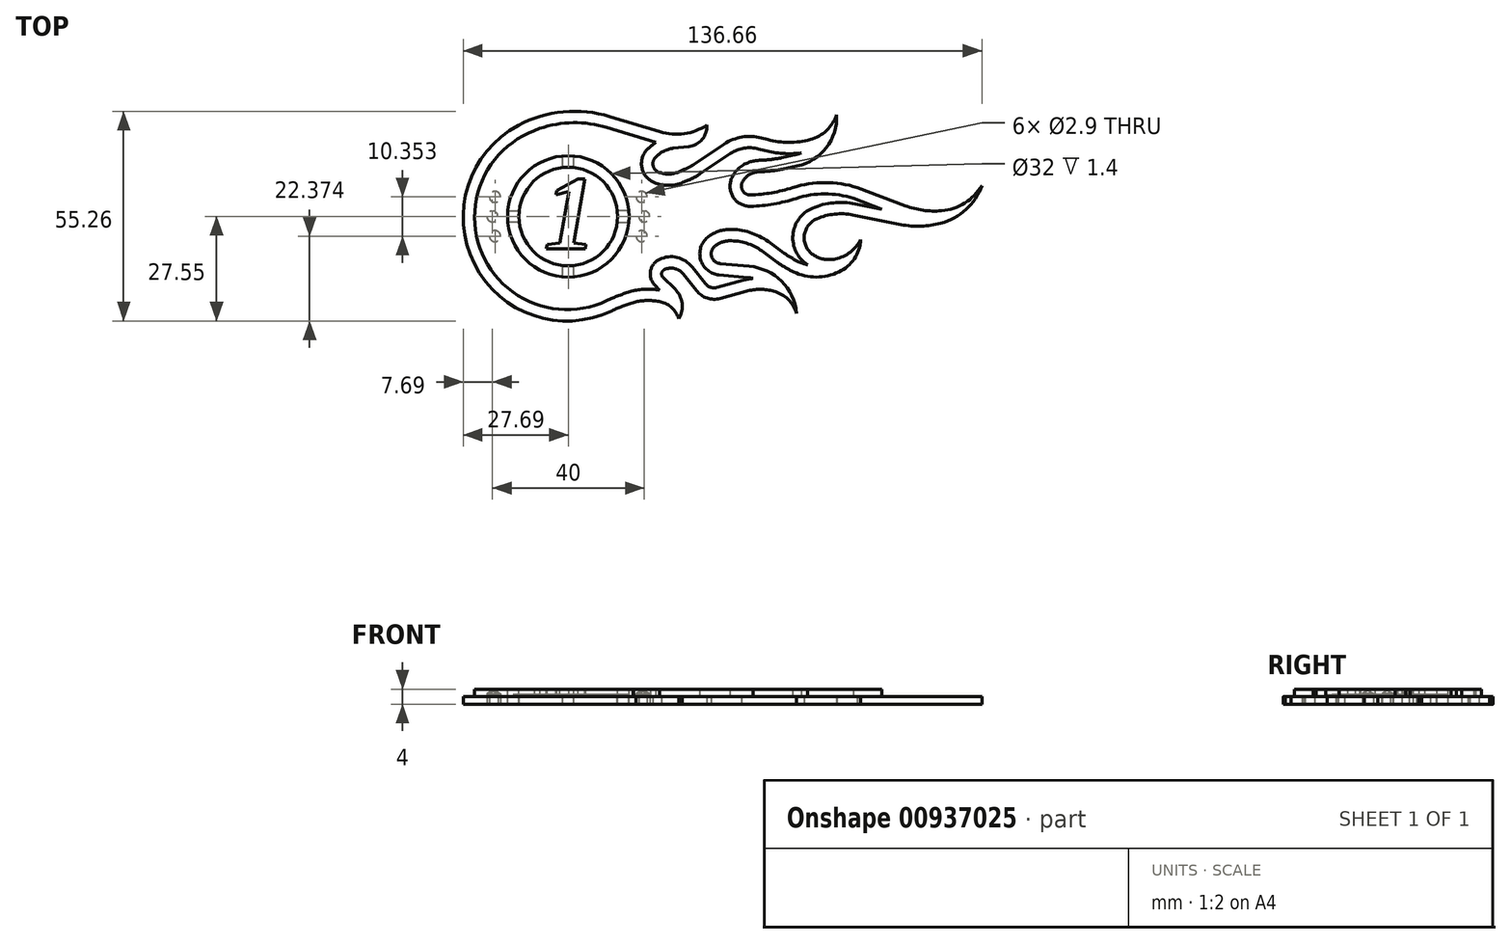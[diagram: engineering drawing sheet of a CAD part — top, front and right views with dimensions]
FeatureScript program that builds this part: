
annotation { "Feature Type Name" : "Feature", "Feature Type Description" : "" }
export const myFeature = defineFeature(function(context is Context, id is Id, definition is map)
    precondition{}
    {
        {
            var Q0;
            Q0=qCreatedBy(makeId("Top.planeOp"),FACE);
            var sketch = newSketch(context, id + "F0", { "sketchPlane" : qUnion([Q0])});
            skArc(sketch, "E0", {"start": v(-15.8, 20.8) * mm, "mid": v(-9.44, 20.3) * mm, "end": v(-3.49, 22.58) * mm});
            skLineSegment(sketch, "E1", {"start": v(-29, 24.82) * mm, "end": v(-15.8, 20.8) * mm});
            skArc(sketch, "E2", {"start": v(-53.14, 22.5) * mm, "mid": v(-64.76, -14.01) * mm, "end": v(-28.48, -26.36) * mm});
            skArc(sketch, "E3", {"start": v(-29, 24.82) * mm, "mid": v(-41.3, 26.06) * mm, "end": v(-53.14, 22.5) * mm});
            skArc(sketch, "E4", {"start": v(-8.25, 16.94) * mm, "mid": v(-4.75, 18.81) * mm, "end": v(-3.49, 22.58) * mm});
            skArc(sketch, "E5", {"start": v(-10.87, -28.44) * mm, "mid": v(-12.7, -25.58) * mm, "end": v(-15.7, -24) * mm});
            skArc(sketch, "E6", {"start": v(-15.7, -24) * mm, "mid": v(-18.94, -23.64) * mm, "end": v(-22.18, -24) * mm});
            skArc(sketch, "E7", {"start": v(-22.18, -24) * mm, "mid": v(-25.39, -25.04) * mm, "end": v(-28.48, -26.36) * mm});
            skArc(sketch, "E8", {"start": v(-10.87, -28.44) * mm, "mid": v(-10.04, -24.35) * mm, "end": v(-11.9, -20.62) * mm});
            skArc(sketch, "E9", {"start": v(-14.69, -15.51) * mm, "mid": v(-15.4, -16.45) * mm, "end": v(-15.02, -17.57) * mm});
            skLineSegment(sketch, "E10", {"start": v(-11.9, -20.62) * mm, "end": v(-15.02, -17.57) * mm});
            skArc(sketch, "E11", {"start": v(-9.7, -16.65) * mm, "mid": v(-12, -15.2) * mm, "end": v(-14.69, -15.51) * mm});
            skLineSegment(sketch, "E12", {"start": v(-9.7, -16.65) * mm, "end": v(-6.22, -21.05) * mm});
            skArc(sketch, "E13", {"start": v(-6.22, -21.05) * mm, "mid": v(-3.42, -23) * mm, "end": v(0, -23.09) * mm});
            skLineSegment(sketch, "E14", {"start": v(-8.25, 16.94) * mm, "end": v(-12.34, 16.47) * mm});
            skArc(sketch, "E15", {"start": v(-12.34, 16.47) * mm, "mid": v(-14.96, 15.66) * mm, "end": v(-17.12, 13.97) * mm});
            skArc(sketch, "E16", {"start": v(-17.12, 13.97) * mm, "mid": v(-17.66, 11.88) * mm, "end": v(-16.27, 10.22) * mm});
            skArc(sketch, "E17", {"start": v(-16.27, 10.22) * mm, "mid": v(-13.63, 9.69) * mm, "end": v(-10.98, 10.22) * mm});
            skLineSegment(sketch, "E18", {"start": v(-10.98, 10.22) * mm, "end": v(-9.42, 10.88) * mm});
            skLineSegment(sketch, "E19", {"start": v(1.1, 17.58) * mm, "end": v(-6.91, 12.23) * mm});
            skArc(sketch, "E20.filletArc", {"start": v(-9.42, 10.88) * mm, "mid": v(-8.13, 11.5) * mm, "end": v(-6.91, 12.23) * mm});
            skArc(sketch, "E21", {"start": v(10.9, 19.2) * mm, "mid": v(5.82, 19.45) * mm, "end": v(1.1, 17.58) * mm});
            skLineSegment(sketch, "E22", {"start": v(10.9, 19.2) * mm, "end": v(12.5, 18.78) * mm});
            skArc(sketch, "E23", {"start": v(12.5, 18.78) * mm, "mid": v(18.13, 18.04) * mm, "end": v(23.76, 18.78) * mm});
            skArc(sketch, "E24", {"start": v(23.76, 18.78) * mm, "mid": v(28.06, 21.17) * mm, "end": v(30.72, 25.31) * mm});
            skArc(sketch, "E25", {"start": v(20.3, 11.8) * mm, "mid": v(27.98, 16.65) * mm, "end": v(30.72, 25.31) * mm});
            skLineSegment(sketch, "E26", {"start": v(20.3, 11.8) * mm, "end": v(16.86, 11.06) * mm});
            skArc(sketch, "E27", {"start": v(10.82, 10.32) * mm, "mid": v(13.86, 10.55) * mm, "end": v(16.86, 11.06) * mm});
            skArc(sketch, "E28", {"start": v(10.82, 10.32) * mm, "mid": v(9.84, 10.23) * mm, "end": v(8.87, 10.03) * mm});
            skArc(sketch, "E29", {"start": v(8.87, 10.03) * mm, "mid": v(7.03, 9.04) * mm, "end": v(5.8, 7.34) * mm});
            skArc(sketch, "E30", {"start": v(5.8, 7.34) * mm, "mid": v(6.02, 5.16) * mm, "end": v(7.97, 4.17) * mm});
            skArc(sketch, "E31", {"start": v(19.12, 6.1) * mm, "mid": v(13.61, 4.74) * mm, "end": v(7.97, 4.17) * mm});
            skArc(sketch, "E32", {"start": v(36.14, 6.1) * mm, "mid": v(27.63, 7.44) * mm, "end": v(19.12, 6.1) * mm});
            skLineSegment(sketch, "E33", {"start": v(0, -23.09) * mm, "end": v(6.9, -21.19) * mm});
            skArc(sketch, "E34", {"start": v(14.19, -21.19) * mm, "mid": v(10.54, -20.7) * mm, "end": v(6.9, -21.19) * mm});
            skArc(sketch, "E35", {"start": v(20.17, -27.02) * mm, "mid": v(17.93, -23.33) * mm, "end": v(14.19, -21.19) * mm});
            skArc(sketch, "E36", {"start": v(20.17, -27.02) * mm, "mid": v(16.15, -18.57) * mm, "end": v(7.68, -14.62) * mm});
            skLineSegment(sketch, "E37", {"start": v(7.68, -14.62) * mm, "end": v(0, -13.91) * mm});
            skArc(sketch, "E38", {"start": v(-1.39, -9.32) * mm, "mid": v(-2.24, -12.08) * mm, "end": v(0, -13.91) * mm});
            skArc(sketch, "E39", {"start": v(2.46, -7.92) * mm, "mid": v(0.42, -8.3) * mm, "end": v(-1.39, -9.32) * mm});
            skArc(sketch, "E40", {"start": v(10.98, -10.59) * mm, "mid": v(6.94, -8.56) * mm, "end": v(2.46, -7.92) * mm});
            skLineSegment(sketch, "E41", {"start": v(10.98, -10.59) * mm, "end": v(15.06, -13.54) * mm});
            skArc(sketch, "E42", {"start": v(15.06, -13.54) * mm, "mid": v(17.16, -14.93) * mm, "end": v(19.37, -16.1) * mm});
            skArc(sketch, "E43", {"start": v(19.37, -16.1) * mm, "mid": v(25.34, -17.46) * mm, "end": v(31.3, -16.1) * mm});
            skArc(sketch, "E44", {"start": v(31.3, -16.1) * mm, "mid": v(35.34, -12.64) * mm, "end": v(37.05, -7.6) * mm});
            skArc(sketch, "E45", {"start": v(30.4, -12.7) * mm, "mid": v(34.29, -10.88) * mm, "end": v(37.05, -7.6) * mm});
            skArc(sketch, "E46", {"start": v(24.84, -11.81) * mm, "mid": v(27.53, -12.78) * mm, "end": v(30.4, -12.7) * mm});
            skArc(sketch, "E47", {"start": v(25.48, -2.1) * mm, "mid": v(22.17, -6.76) * mm, "end": v(24.84, -11.81) * mm});
            skArc(sketch, "E48", {"start": v(35.02, -1.1) * mm, "mid": v(30.17, -0.88) * mm, "end": v(25.48, -2.1) * mm});
            skLineSegment(sketch, "E49", {"start": v(35.02, -1.1) * mm, "end": v(47.7, -3.63) * mm});
            skArc(sketch, "E50", {"start": v(47.7, -3.63) * mm, "mid": v(52.94, -4.06) * mm, "end": v(58.13, -3.3) * mm});
            skArc(sketch, "E51", {"start": v(58.13, -3.3) * mm, "mid": v(64.79, 0.34) * mm, "end": v(68.97, 6.67) * mm});
            skArc(sketch, "E52", {"start": v(58.36, 0) * mm, "mid": v(64.48, 2.05) * mm, "end": v(68.97, 6.67) * mm});
            skArc(sketch, "E53", {"start": v(48.76, 1.34) * mm, "mid": v(53.49, 0.13) * mm, "end": v(58.36, 0) * mm});
            skLineSegment(sketch, "E54", {"start": v(36.14, 6.1) * mm, "end": v(48.76, 1.34) * mm});
            skArc(sketch, "E55.0", {"start": v(-12.68, 19.45) * mm, "mid": v(-12.7, 19.44) * mm, "end": v(-12.72, 19.44) * mm});
            skLineSegment(sketch, "E56", {"start": v(-16.92, 18) * mm, "end": v(-16.92, 18) * mm});
            skLineSegment(sketch, "E57", {"start": v(-19.37, 15.96) * mm, "end": v(-19.34, 15.99) * mm});
            skSolve(sketch);
        }
        {
            var Q0;
            Q0=qSketchRegion(id+"F0",true);
            extrude(context, id + "F1", {"entities" : qUnion([Q0]), "depth" : 2 * mm, "offsetDistance" : 25 * mm});
        }
        {
            var Q0;
            Q0=makeQuery(id+"F1.opExtrude","CAP_FACE",FACE,{"disambiguationData":[OSD([sQuery(id+"F0.wireOp",EDGE,"E0"),sQuery(id+"F0.wireOp",EDGE,"E1"),sQuery(id+"F0.wireOp",EDGE,"E2"),sQuery(id+"F0.wireOp",EDGE,"E3"),sQuery(id+"F0.wireOp",EDGE,"E4"),sQuery(id+"F0.wireOp",EDGE,"E5"),sQuery(id+"F0.wireOp",EDGE,"E6"),sQuery(id+"F0.wireOp",EDGE,"E7"),sQuery(id+"F0.wireOp",EDGE,"E8"),sQuery(id+"F0.wireOp",EDGE,"E9"),sQuery(id+"F0.wireOp",EDGE,"E10"),sQuery(id+"F0.wireOp",EDGE,"E11"),sQuery(id+"F0.wireOp",EDGE,"E12"),sQuery(id+"F0.wireOp",EDGE,"E13"),sQuery(id+"F0.wireOp",EDGE,"E14"),sQuery(id+"F0.wireOp",EDGE,"E15"),sQuery(id+"F0.wireOp",EDGE,"E16"),sQuery(id+"F0.wireOp",EDGE,"E17"),sQuery(id+"F0.wireOp",EDGE,"E18"),sQuery(id+"F0.wireOp",EDGE,"E19"),sQuery(id+"F0.wireOp",EDGE,"E20.filletArc"),sQuery(id+"F0.wireOp",EDGE,"E21"),sQuery(id+"F0.wireOp",EDGE,"E22"),sQuery(id+"F0.wireOp",EDGE,"E23"),sQuery(id+"F0.wireOp",EDGE,"E24"),sQuery(id+"F0.wireOp",EDGE,"E25"),sQuery(id+"F0.wireOp",EDGE,"E26"),sQuery(id+"F0.wireOp",EDGE,"E27"),sQuery(id+"F0.wireOp",EDGE,"E28"),sQuery(id+"F0.wireOp",EDGE,"E29"),sQuery(id+"F0.wireOp",EDGE,"E30"),sQuery(id+"F0.wireOp",EDGE,"E31"),sQuery(id+"F0.wireOp",EDGE,"E32"),sQuery(id+"F0.wireOp",EDGE,"E33"),sQuery(id+"F0.wireOp",EDGE,"E34"),sQuery(id+"F0.wireOp",EDGE,"E35"),sQuery(id+"F0.wireOp",EDGE,"E36"),sQuery(id+"F0.wireOp",EDGE,"E37"),sQuery(id+"F0.wireOp",EDGE,"E38"),sQuery(id+"F0.wireOp",EDGE,"E39"),sQuery(id+"F0.wireOp",EDGE,"E40"),sQuery(id+"F0.wireOp",EDGE,"E41"),sQuery(id+"F0.wireOp",EDGE,"E42"),sQuery(id+"F0.wireOp",EDGE,"E43"),sQuery(id+"F0.wireOp",EDGE,"E44"),sQuery(id+"F0.wireOp",EDGE,"E45"),sQuery(id+"F0.wireOp",EDGE,"E46"),sQuery(id+"F0.wireOp",EDGE,"E47"),sQuery(id+"F0.wireOp",EDGE,"E48"),sQuery(id+"F0.wireOp",EDGE,"E49"),sQuery(id+"F0.wireOp",EDGE,"E50"),sQuery(id+"F0.wireOp",EDGE,"E51"),sQuery(id+"F0.wireOp",EDGE,"E52"),sQuery(id+"F0.wireOp",EDGE,"E53"),sQuery(id+"F0.wireOp",EDGE,"E54")])],"isStart":false});
            var sketch = newSketch(context, id + "F2", { "sketchPlane" : qUnion([Q0])});
            skArc(sketch, "E58", {"start": v(-24.07, -3) * mm, "mid": v(-24, -1.5) * mm, "end": v(-24.07, 0) * mm});
            skArc(sketch, "E59", {"start": v(-27.09, -3) * mm, "mid": v(-27, -1.5) * mm, "end": v(-27.09, 0) * mm});
            skArc(sketch, "E60", {"start": v(-38.5, 11.41) * mm, "mid": v(-40, 11.5) * mm, "end": v(-41.5, 11.41) * mm});
            skArc(sketch, "E61", {"start": v(-38.5, 14.43) * mm, "mid": v(-40, 14.5) * mm, "end": v(-41.5, 14.43) * mm});
            skArc(sketch, "E62", {"start": v(-41.5, -14.41) * mm, "mid": v(-40, -14.5) * mm, "end": v(-38.5, -14.41) * mm});
            skArc(sketch, "E63", {"start": v(-41.5, -17.43) * mm, "mid": v(-40, -17.5) * mm, "end": v(-38.5, -17.43) * mm});
            skArc(sketch, "E64", {"start": v(-55.93, 0) * mm, "mid": v(-56, -1.5) * mm, "end": v(-55.93, -3) * mm});
            skArc(sketch, "E65", {"start": v(-52.91, 0.02) * mm, "mid": v(-53, -1.5) * mm, "end": v(-52.91, -3) * mm});
            skLineSegment(sketch, "E66", {"start": v(-41.5, -17.43) * mm, "end": v(-41.5, -14.41) * mm});
            skLineSegment(sketch, "E67", {"start": v(-38.5, -17.43) * mm, "end": v(-38.5, -14.41) * mm});
            skLineSegment(sketch, "E68", {"start": v(-27.09, -3) * mm, "end": v(-24.07, -3) * mm});
            skLineSegment(sketch, "E69", {"start": v(-24.07, 0) * mm, "end": v(-27.09, 0) * mm});
            skLineSegment(sketch, "E70", {"start": v(-38.5, 11.41) * mm, "end": v(-38.5, 14.43) * mm});
            skLineSegment(sketch, "E71", {"start": v(-41.5, 11.41) * mm, "end": v(-41.5, 14.43) * mm});
            skLineSegment(sketch, "E72", {"start": v(-52.91, -3) * mm, "end": v(-55.93, -3) * mm});
            skLineSegment(sketch, "E73", {"start": v(-55.93, 0) * mm, "end": v(-52.91, 0.02) * mm});
            skSolve(sketch);
        }
        {
            var Q0;
            Q0=makeQuery(id+"F1.opExtrude","CAP_FACE",FACE,{"disambiguationData":[OSD([sQuery(id+"F0.wireOp",EDGE,"E0"),sQuery(id+"F0.wireOp",EDGE,"E1"),sQuery(id+"F0.wireOp",EDGE,"E2"),sQuery(id+"F0.wireOp",EDGE,"E3"),sQuery(id+"F0.wireOp",EDGE,"E4"),sQuery(id+"F0.wireOp",EDGE,"E5"),sQuery(id+"F0.wireOp",EDGE,"E6"),sQuery(id+"F0.wireOp",EDGE,"E7"),sQuery(id+"F0.wireOp",EDGE,"E8"),sQuery(id+"F0.wireOp",EDGE,"E9"),sQuery(id+"F0.wireOp",EDGE,"E10"),sQuery(id+"F0.wireOp",EDGE,"E11"),sQuery(id+"F0.wireOp",EDGE,"E12"),sQuery(id+"F0.wireOp",EDGE,"E13"),sQuery(id+"F0.wireOp",EDGE,"E14"),sQuery(id+"F0.wireOp",EDGE,"E15"),sQuery(id+"F0.wireOp",EDGE,"E16"),sQuery(id+"F0.wireOp",EDGE,"E17"),sQuery(id+"F0.wireOp",EDGE,"E18"),sQuery(id+"F0.wireOp",EDGE,"E19"),sQuery(id+"F0.wireOp",EDGE,"E20.filletArc"),sQuery(id+"F0.wireOp",EDGE,"E21"),sQuery(id+"F0.wireOp",EDGE,"E22"),sQuery(id+"F0.wireOp",EDGE,"E23"),sQuery(id+"F0.wireOp",EDGE,"E24"),sQuery(id+"F0.wireOp",EDGE,"E25"),sQuery(id+"F0.wireOp",EDGE,"E26"),sQuery(id+"F0.wireOp",EDGE,"E27"),sQuery(id+"F0.wireOp",EDGE,"E28"),sQuery(id+"F0.wireOp",EDGE,"E29"),sQuery(id+"F0.wireOp",EDGE,"E30"),sQuery(id+"F0.wireOp",EDGE,"E31"),sQuery(id+"F0.wireOp",EDGE,"E32"),sQuery(id+"F0.wireOp",EDGE,"E33"),sQuery(id+"F0.wireOp",EDGE,"E34"),sQuery(id+"F0.wireOp",EDGE,"E35"),sQuery(id+"F0.wireOp",EDGE,"E36"),sQuery(id+"F0.wireOp",EDGE,"E37"),sQuery(id+"F0.wireOp",EDGE,"E38"),sQuery(id+"F0.wireOp",EDGE,"E39"),sQuery(id+"F0.wireOp",EDGE,"E40"),sQuery(id+"F0.wireOp",EDGE,"E41"),sQuery(id+"F0.wireOp",EDGE,"E42"),sQuery(id+"F0.wireOp",EDGE,"E43"),sQuery(id+"F0.wireOp",EDGE,"E44"),sQuery(id+"F0.wireOp",EDGE,"E45"),sQuery(id+"F0.wireOp",EDGE,"E46"),sQuery(id+"F0.wireOp",EDGE,"E47"),sQuery(id+"F0.wireOp",EDGE,"E48"),sQuery(id+"F0.wireOp",EDGE,"E49"),sQuery(id+"F0.wireOp",EDGE,"E50"),sQuery(id+"F0.wireOp",EDGE,"E51"),sQuery(id+"F0.wireOp",EDGE,"E52"),sQuery(id+"F0.wireOp",EDGE,"E53"),sQuery(id+"F0.wireOp",EDGE,"E54")])],"isStart":false});
            var sketch = newSketch(context, id + "F3", { "sketchPlane" : qUnion([Q0])});
            skArc(sketch, "E74.0", {"start": v(-29.87, 21.95) * mm, "mid": v(-38.73, 23.2) * mm, "end": v(-47.54, 21.67) * mm});
            skArc(sketch, "E75", {"start": v(-48.94, 21.12) * mm, "mid": v(-62.73, -11.25) * mm, "end": v(-29.8, -23.67) * mm});
            skLineSegment(sketch, "E76", {"start": v(-48.94, 21.12) * mm, "end": v(-47.54, 21.67) * mm});
            skLineSegment(sketch, "E77.0", {"start": v(-29.87, 21.95) * mm, "end": v(-16.92, 18) * mm});
            skLineSegment(sketch, "E78", {"start": v(-20.59, 18.76) * mm, "end": v(-20.59, 18.76) * mm});
            skArc(sketch, "E79", {"start": v(-16.92, 18) * mm, "mid": v(-18.2, 17.08) * mm, "end": v(-19.34, 15.99) * mm});
            skArc(sketch, "E80.0", {"start": v(-19.37, 15.96) * mm, "mid": v(-20.58, 11.21) * mm, "end": v(-17.43, 7.46) * mm});
            skArc(sketch, "E81.0", {"start": v(-17.43, 7.46) * mm, "mid": v(-13.63, 6.69) * mm, "end": v(-9.82, 7.46) * mm});
            skLineSegment(sketch, "E82.0", {"start": v(-9.82, 7.46) * mm, "end": v(-8.25, 8.12) * mm});
            skArc(sketch, "E83.0", {"start": v(-8.25, 8.12) * mm, "mid": v(-6.71, 8.86) * mm, "end": v(-5.25, 9.74) * mm});
            skLineSegment(sketch, "E84.0", {"start": v(2.76, 15.09) * mm, "end": v(-5.25, 9.74) * mm});
            skArc(sketch, "E85.0", {"start": v(10.13, 16.3) * mm, "mid": v(6.31, 16.5) * mm, "end": v(2.76, 15.09) * mm});
            skLineSegment(sketch, "E86.0", {"start": v(10.13, 16.3) * mm, "end": v(11.74, 15.88) * mm});
            skArc(sketch, "E87.0", {"start": v(11.74, 15.88) * mm, "mid": v(16.51, 15.1) * mm, "end": v(21.35, 15.25) * mm});
            skLineSegment(sketch, "E88.0", {"start": v(19.3, 14.65) * mm, "end": v(16.22, 13.99) * mm});
            skArc(sketch, "E89.0", {"start": v(19.66, 14.73) * mm, "mid": v(20.52, 14.95) * mm, "end": v(21.35, 15.25) * mm});
            skArc(sketch, "E90.0", {"start": v(10.73, 13.32) * mm, "mid": v(13.5, 13.53) * mm, "end": v(16.22, 13.99) * mm});
            skArc(sketch, "E91.0", {"start": v(10.73, 13.32) * mm, "mid": v(9.4, 13.2) * mm, "end": v(8.08, 12.92) * mm});
            skArc(sketch, "E92.0", {"start": v(8.08, 12.92) * mm, "mid": v(5.05, 11.3) * mm, "end": v(3.04, 8.52) * mm});
            skArc(sketch, "E93.0", {"start": v(3.04, 8.52) * mm, "mid": v(3.54, 3.47) * mm, "end": v(8.07, 1.17) * mm});
            skArc(sketch, "E94.0", {"start": v(20.04, 3.24) * mm, "mid": v(14.12, 1.79) * mm, "end": v(8.07, 1.17) * mm});
            skLineSegment(sketch, "E95.0", {"start": v(35.6, 1.84) * mm, "end": v(42.66, 0.43) * mm});
            skArc(sketch, "E96.0", {"start": v(35.6, 1.84) * mm, "mid": v(29.87, 2.1) * mm, "end": v(24.3, 0.67) * mm});
            skArc(sketch, "E97.0", {"start": v(24.3, 0.67) * mm, "mid": v(19.19, -6.38) * mm, "end": v(23, -14.2) * mm});
            skArc(sketch, "E98.0", {"start": v(20.66, -13.4) * mm, "mid": v(21.81, -13.87) * mm, "end": v(23, -14.2) * mm});
            skArc(sketch, "E99.0", {"start": v(16.82, -11.12) * mm, "mid": v(18.69, -12.35) * mm, "end": v(20.66, -13.4) * mm});
            skLineSegment(sketch, "E100.0", {"start": v(12.74, -8.16) * mm, "end": v(16.82, -11.12) * mm});
            skArc(sketch, "E101.0", {"start": v(12.74, -8.16) * mm, "mid": v(7.83, -5.7) * mm, "end": v(2.4, -4.92) * mm});
            skArc(sketch, "E102.0", {"start": v(2.4, -4.92) * mm, "mid": v(-0.61, -5.48) * mm, "end": v(-3.27, -7) * mm});
            skArc(sketch, "E103.0", {"start": v(-3.27, -7) * mm, "mid": v(-5.11, -12.95) * mm, "end": v(-0.27, -16.9) * mm});
            skLineSegment(sketch, "E104.0", {"start": v(7.4, -17.6) * mm, "end": v(-0.27, -16.9) * mm});
            skLineSegment(sketch, "E105.0", {"start": v(-0.8, -20.2) * mm, "end": v(6.1, -18.3) * mm});
            skArc(sketch, "E106", {"start": v(8.67, -17.8) * mm, "mid": v(8.04, -17.68) * mm, "end": v(7.4, -17.6) * mm});
            skArc(sketch, "E107", {"start": v(8.67, -17.8) * mm, "mid": v(7.38, -18) * mm, "end": v(6.1, -18.3) * mm});
            skArc(sketch, "E108.0", {"start": v(-3.87, -19.2) * mm, "mid": v(-2.48, -20.16) * mm, "end": v(-0.8, -20.2) * mm});
            skLineSegment(sketch, "E109.0", {"start": v(-7.35, -14.8) * mm, "end": v(-3.87, -19.2) * mm});
            skArc(sketch, "E110.0", {"start": v(-7.35, -14.8) * mm, "mid": v(-11.32, -12.28) * mm, "end": v(-16, -12.81) * mm});
            skArc(sketch, "E111.0", {"start": v(-16, -12.81) * mm, "mid": v(-18.35, -15.97) * mm, "end": v(-17.12, -19.72) * mm});
            skLineSegment(sketch, "E112.0", {"start": v(-15.9, -20.9) * mm, "end": v(-17.12, -19.72) * mm});
            skArc(sketch, "E113.0", {"start": v(-15.9, -20.9) * mm, "mid": v(-19.4, -20.64) * mm, "end": v(-22.85, -21.08) * mm});
            skArc(sketch, "E114.0", {"start": v(-22.98, -21.11) * mm, "mid": v(-26.29, -22.18) * mm, "end": v(-29.49, -23.52) * mm});
            skLineSegment(sketch, "E115", {"start": v(-22.98, -21.11) * mm, "end": v(-22.85, -21.08) * mm});
            skLineSegment(sketch, "E116", {"start": v(19.3, 14.65) * mm, "end": v(19.66, 14.73) * mm});
            skLineSegment(sketch, "E117", {"start": v(-19.37, 15.96) * mm, "end": v(-19.34, 15.99) * mm});
            skArc(sketch, "E118", {"start": v(35.15, 3.27) * mm, "mid": v(27.6, 4.44) * mm, "end": v(20.04, 3.24) * mm});
            skLineSegment(sketch, "E119", {"start": v(35.15, 3.27) * mm, "end": v(42.66, 0.43) * mm});
            skLineSegment(sketch, "E120", {"start": v(-29.8, -23.67) * mm, "end": v(-29.49, -23.52) * mm});
            skSolve(sketch);
        }
        {
            var Q0;
            Q0 = qSketchRegion(id + "F2", true);
            extrude(context, id + "F4", {"entities" : qUnion([Q0]), "operationType" : NewBodyOperationType.REMOVE, "oppositeDirection" : true, "depth" : 2 * mm, "offsetDistance" : 25 * mm});
        }
        {
            var Q0;
            Q0 = qSketchRegion(id + "F3", true);
            extrude(context, id + "F5", {"entities" : qUnion([Q0]), "operationType" : NewBodyOperationType.ADD, "depth" : 2 * mm, "offsetDistance" : 25 * mm});
        }
        {
            var Q0;
            Q0=makeQuery(id+"F5.opExtrude","CAP_FACE",FACE,{"disambiguationData":[OSD([sQuery(id+"F3.wireOp",EDGE,"E74.0"),sQuery(id+"F3.wireOp",EDGE,"E75"),sQuery(id+"F3.wireOp",EDGE,"E76"),sQuery(id+"F3.wireOp",EDGE,"E77.0"),sQuery(id+"F3.wireOp",EDGE,"E79"),sQuery(id+"F3.wireOp",EDGE,"E80.0"),sQuery(id+"F3.wireOp",EDGE,"E81.0"),sQuery(id+"F3.wireOp",EDGE,"E82.0"),sQuery(id+"F3.wireOp",EDGE,"E83.0"),sQuery(id+"F3.wireOp",EDGE,"E84.0"),sQuery(id+"F3.wireOp",EDGE,"E85.0"),sQuery(id+"F3.wireOp",EDGE,"E86.0"),sQuery(id+"F3.wireOp",EDGE,"E87.0"),sQuery(id+"F3.wireOp",EDGE,"E88.0"),sQuery(id+"F3.wireOp",EDGE,"E89.0"),sQuery(id+"F3.wireOp",EDGE,"E90.0"),sQuery(id+"F3.wireOp",EDGE,"E91.0"),sQuery(id+"F3.wireOp",EDGE,"E92.0"),sQuery(id+"F3.wireOp",EDGE,"E93.0"),sQuery(id+"F3.wireOp",EDGE,"E94.0"),sQuery(id+"F3.wireOp",EDGE,"E95.0"),sQuery(id+"F3.wireOp",EDGE,"E96.0"),sQuery(id+"F3.wireOp",EDGE,"E97.0"),sQuery(id+"F3.wireOp",EDGE,"E98.0"),sQuery(id+"F3.wireOp",EDGE,"E99.0"),sQuery(id+"F3.wireOp",EDGE,"E100.0"),sQuery(id+"F3.wireOp",EDGE,"E101.0"),sQuery(id+"F3.wireOp",EDGE,"E102.0"),sQuery(id+"F3.wireOp",EDGE,"E103.0"),sQuery(id+"F3.wireOp",EDGE,"E104.0"),sQuery(id+"F3.wireOp",EDGE,"E105.0"),sQuery(id+"F3.wireOp",EDGE,"E106"),sQuery(id+"F3.wireOp",EDGE,"E107"),sQuery(id+"F3.wireOp",EDGE,"E108.0"),sQuery(id+"F3.wireOp",EDGE,"E109.0"),sQuery(id+"F3.wireOp",EDGE,"E110.0"),sQuery(id+"F3.wireOp",EDGE,"E111.0"),sQuery(id+"F3.wireOp",EDGE,"E112.0"),sQuery(id+"F3.wireOp",EDGE,"E113.0"),sQuery(id+"F3.wireOp",EDGE,"E114.0"),sQuery(id+"F3.wireOp",EDGE,"E115"),sQuery(id+"F3.wireOp",EDGE,"E116"),sQuery(id+"F3.wireOp",EDGE,"E117"),sQuery(id+"F3.wireOp",EDGE,"E118"),sQuery(id+"F3.wireOp",EDGE,"E119"),sQuery(id+"F3.wireOp",EDGE,"E120")])],"isStart":false});
            var sketch = newSketch(context, id + "F6", { "sketchPlane" : qUnion([Q0])});
            skCircle(sketch, "E121", {"center": v(-40, -1.5) * mm, "radius": 16 * mm});
            skCircle(sketch, "E122", {"center": v(-40, -1.5) * mm, "radius": 13 * mm});
            skSolve(sketch);
        }
        {
            var Q0;
            Q0 = qSketchRegion(id + "F6", true);
            extrude(context, id + "F7", {"entities" : qUnion([Q0]), "operationType" : NewBodyOperationType.REMOVE, "oppositeDirection" : true, "depth" : 1.4 * mm, "offsetDistance" : 25 * mm});
        }
        {
            var Q0;
            Q0=makeQuery(id+"F6.imprint","IMPRINT",FACE,{"disambiguationData":[TD([[makeQuery(id+"F6.imprint","IMPRINT",EDGE,{"derivedFrom":sQuery(id+"F6.wireOp",EDGE,"E121")}),-1.0]])]});
            var sketch = newSketch(context, id + "F8", { "sketchPlane" : qUnion([Q0])});
            skText(sketch, "E123", { "text": "1", "fontName": "Tinos-BoldItalic.ttf"});
            const initialGuessF8  = {"E123": [-0.0464, -0.01, 1, 0, 0.02]};
            skSetInitialGuess(sketch, initialGuessF8);
            skSolve(sketch);
        }
        {
            var Q0;
            Q0 = qSketchRegion(id + "F8", true);
            extrude(context, id + "F9", {"entities" : qUnion([Q0]), "operationType" : NewBodyOperationType.REMOVE, "oppositeDirection" : true, "depth" : 1.4 * mm, "offsetDistance" : 25 * mm});
        }
        {
            var Q0;
            Q0=makeQuery(id+"F1.opExtrude","CAP_FACE",FACE,{"disambiguationData":[OSD([sQuery(id+"F0.wireOp",EDGE,"E0"),sQuery(id+"F0.wireOp",EDGE,"E1"),sQuery(id+"F0.wireOp",EDGE,"E2"),sQuery(id+"F0.wireOp",EDGE,"E3"),sQuery(id+"F0.wireOp",EDGE,"E4"),sQuery(id+"F0.wireOp",EDGE,"E5"),sQuery(id+"F0.wireOp",EDGE,"E6"),sQuery(id+"F0.wireOp",EDGE,"E7"),sQuery(id+"F0.wireOp",EDGE,"E8"),sQuery(id+"F0.wireOp",EDGE,"E9"),sQuery(id+"F0.wireOp",EDGE,"E10"),sQuery(id+"F0.wireOp",EDGE,"E11"),sQuery(id+"F0.wireOp",EDGE,"E12"),sQuery(id+"F0.wireOp",EDGE,"E13"),sQuery(id+"F0.wireOp",EDGE,"E14"),sQuery(id+"F0.wireOp",EDGE,"E15"),sQuery(id+"F0.wireOp",EDGE,"E16"),sQuery(id+"F0.wireOp",EDGE,"E17"),sQuery(id+"F0.wireOp",EDGE,"E18"),sQuery(id+"F0.wireOp",EDGE,"E19"),sQuery(id+"F0.wireOp",EDGE,"E20.filletArc"),sQuery(id+"F0.wireOp",EDGE,"E21"),sQuery(id+"F0.wireOp",EDGE,"E22"),sQuery(id+"F0.wireOp",EDGE,"E23"),sQuery(id+"F0.wireOp",EDGE,"E24"),sQuery(id+"F0.wireOp",EDGE,"E25"),sQuery(id+"F0.wireOp",EDGE,"E26"),sQuery(id+"F0.wireOp",EDGE,"E27"),sQuery(id+"F0.wireOp",EDGE,"E28"),sQuery(id+"F0.wireOp",EDGE,"E29"),sQuery(id+"F0.wireOp",EDGE,"E30"),sQuery(id+"F0.wireOp",EDGE,"E31"),sQuery(id+"F0.wireOp",EDGE,"E32"),sQuery(id+"F0.wireOp",EDGE,"E33"),sQuery(id+"F0.wireOp",EDGE,"E34"),sQuery(id+"F0.wireOp",EDGE,"E35"),sQuery(id+"F0.wireOp",EDGE,"E36"),sQuery(id+"F0.wireOp",EDGE,"E37"),sQuery(id+"F0.wireOp",EDGE,"E38"),sQuery(id+"F0.wireOp",EDGE,"E39"),sQuery(id+"F0.wireOp",EDGE,"E40"),sQuery(id+"F0.wireOp",EDGE,"E41"),sQuery(id+"F0.wireOp",EDGE,"E42"),sQuery(id+"F0.wireOp",EDGE,"E43"),sQuery(id+"F0.wireOp",EDGE,"E44"),sQuery(id+"F0.wireOp",EDGE,"E45"),sQuery(id+"F0.wireOp",EDGE,"E46"),sQuery(id+"F0.wireOp",EDGE,"E47"),sQuery(id+"F0.wireOp",EDGE,"E48"),sQuery(id+"F0.wireOp",EDGE,"E49"),sQuery(id+"F0.wireOp",EDGE,"E50"),sQuery(id+"F0.wireOp",EDGE,"E51"),sQuery(id+"F0.wireOp",EDGE,"E52"),sQuery(id+"F0.wireOp",EDGE,"E53"),sQuery(id+"F0.wireOp",EDGE,"E54")])],"isStart":true});
            var sketch = newSketch(context, id + "F10", { "sketchPlane" : qUnion([Q0])});
            skPoint(sketch, "E124", {"position": v(-60, 1.5) * mm});
            skPoint(sketch, "E125", {"position": v(-20, 1.5) * mm});
            skLineSegment(sketch, "E126", {"start": v(-59.32, 6.68) * mm, "end": v(-20.68, -3.68) * mm});
            skPoint(sketch, "E127.orphan", {"position": v(-40, 1.5) * mm});
            skCircle(sketch, "E128", {"center": v(-40, 1.5) * mm, "radius": 20 * mm});
            skLineSegment(sketch, "E129", {"start": v(-59.32, -3.68) * mm, "end": v(-20.68, 6.68) * mm});
            skPoint(sketch, "E130", {"position": v(-59.32, 6.68) * mm});
            skPoint(sketch, "E131", {"position": v(-59.32, -3.68) * mm});
            skPoint(sketch, "E132", {"position": v(-20.68, 6.68) * mm});
            skPoint(sketch, "E133", {"position": v(-20.68, -3.68) * mm});
            skSolve(sketch);
        }
        {
            var Q0;
            Q0=sQuery(id+"F10.wireOp",VERTEX,"E124");
            var Q1;
            Q1=sQuery(id+"F10.wireOp",VERTEX,"E125");
            var Q2;
            Q2=sQuery(id+"F10.wireOp",VERTEX,"E130");
            var Q3;
            Q3=sQuery(id+"F10.wireOp",VERTEX,"E131");
            var Q4;
            Q4=sQuery(id+"F10.wireOp",VERTEX,"E132");
            var Q5;
            Q5=sQuery(id+"F10.wireOp",VERTEX,"E133");
            var Q6;
            Q6=makeQuery(id+"F1.opExtrude","SWEPT_BODY",BODY,{"disambiguationData":[OSD([sQuery(id+"F0.wireOp",EDGE,"E0"),sQuery(id+"F0.wireOp",EDGE,"E1"),sQuery(id+"F0.wireOp",EDGE,"E2"),sQuery(id+"F0.wireOp",EDGE,"E3"),sQuery(id+"F0.wireOp",EDGE,"E4"),sQuery(id+"F0.wireOp",EDGE,"E5"),sQuery(id+"F0.wireOp",EDGE,"E6"),sQuery(id+"F0.wireOp",EDGE,"E7"),sQuery(id+"F0.wireOp",EDGE,"E8"),sQuery(id+"F0.wireOp",EDGE,"E9"),sQuery(id+"F0.wireOp",EDGE,"E10"),sQuery(id+"F0.wireOp",EDGE,"E11"),sQuery(id+"F0.wireOp",EDGE,"E12"),sQuery(id+"F0.wireOp",EDGE,"E13"),sQuery(id+"F0.wireOp",EDGE,"E14"),sQuery(id+"F0.wireOp",EDGE,"E15"),sQuery(id+"F0.wireOp",EDGE,"E16"),sQuery(id+"F0.wireOp",EDGE,"E17"),sQuery(id+"F0.wireOp",EDGE,"E18"),sQuery(id+"F0.wireOp",EDGE,"E19"),sQuery(id+"F0.wireOp",EDGE,"E20.filletArc"),sQuery(id+"F0.wireOp",EDGE,"E21"),sQuery(id+"F0.wireOp",EDGE,"E22"),sQuery(id+"F0.wireOp",EDGE,"E23"),sQuery(id+"F0.wireOp",EDGE,"E24"),sQuery(id+"F0.wireOp",EDGE,"E25"),sQuery(id+"F0.wireOp",EDGE,"E26"),sQuery(id+"F0.wireOp",EDGE,"E27"),sQuery(id+"F0.wireOp",EDGE,"E28"),sQuery(id+"F0.wireOp",EDGE,"E29"),sQuery(id+"F0.wireOp",EDGE,"E30"),sQuery(id+"F0.wireOp",EDGE,"E31"),sQuery(id+"F0.wireOp",EDGE,"E32"),sQuery(id+"F0.wireOp",EDGE,"E33"),sQuery(id+"F0.wireOp",EDGE,"E34"),sQuery(id+"F0.wireOp",EDGE,"E35"),sQuery(id+"F0.wireOp",EDGE,"E36"),sQuery(id+"F0.wireOp",EDGE,"E37"),sQuery(id+"F0.wireOp",EDGE,"E38"),sQuery(id+"F0.wireOp",EDGE,"E39"),sQuery(id+"F0.wireOp",EDGE,"E40"),sQuery(id+"F0.wireOp",EDGE,"E41"),sQuery(id+"F0.wireOp",EDGE,"E42"),sQuery(id+"F0.wireOp",EDGE,"E43"),sQuery(id+"F0.wireOp",EDGE,"E44"),sQuery(id+"F0.wireOp",EDGE,"E45"),sQuery(id+"F0.wireOp",EDGE,"E46"),sQuery(id+"F0.wireOp",EDGE,"E47"),sQuery(id+"F0.wireOp",EDGE,"E48"),sQuery(id+"F0.wireOp",EDGE,"E49"),sQuery(id+"F0.wireOp",EDGE,"E50"),sQuery(id+"F0.wireOp",EDGE,"E51"),sQuery(id+"F0.wireOp",EDGE,"E52"),sQuery(id+"F0.wireOp",EDGE,"E53"),sQuery(id+"F0.wireOp",EDGE,"E54")])]});
            hole(context, id + "F11", {"style" : HoleStyle.SIMPLE, "endStyle" : HoleEndStyle.BLIND, "holeDiameter" : 2.9 * mm, "majorDiameter" : 5 * mm, "holeDepth" : 2.8 * mm, "isTappedThrough" : true, "tappedDepth" : 12 * mm, "tapClearance" : 3, "startFromSketch" : true, "locations" : qUnion([Q0, Q1, Q2, Q3, Q4, Q5]), "scope" : qUnion([Q6])});
        }
    });
